# Revit family: Wrestling_Mat_Storage-PSS-4091
name_source: partatom
category: Specialty Equipment
revit_build: Autodesk Revit 2017 (Build: 20170816_0615(x64)
units: mm (PartAtom-declared; Revit-internal decimal feet)

## family parameters
Always vertical = Yes
Cut with Voids When Loaded = No
OmniClass Number = 23.40.50.34.34
OmniClass Title = Equipment Storage Racks
Part Type = Normal
Room Calculation Point = No
Round Connector Dimension = Use Diameter
Shared = No
Work Plane-Based = No

## types (1)
- Wrestling_Mat_Storage-PSS-4091
    Assembly Code = E1020900
    BIM Version = v3.1
    CSI MasterFormat = 11 66 23
    Description = Wrestling Mat Storage System
    Length = 20' - 0"
    Manufacturer = Performance Sports Systems
    Mat Color = Generic - Wrestling Mat
    Model = 4091
    Product Page URL = http://www.perfsports.com
    Sling Material = Vinyl Coated Fabric - Performance Sports Systems - C04 Royal Blue
    Superstructure Finish = Powder Coat - Performance Sports Systems - Black
    URL = http://www.perfsports.com

## geometry (parser evidence)
native form markers: Blend x60, Sweep x5
no freeform markers — native parametric forms only
